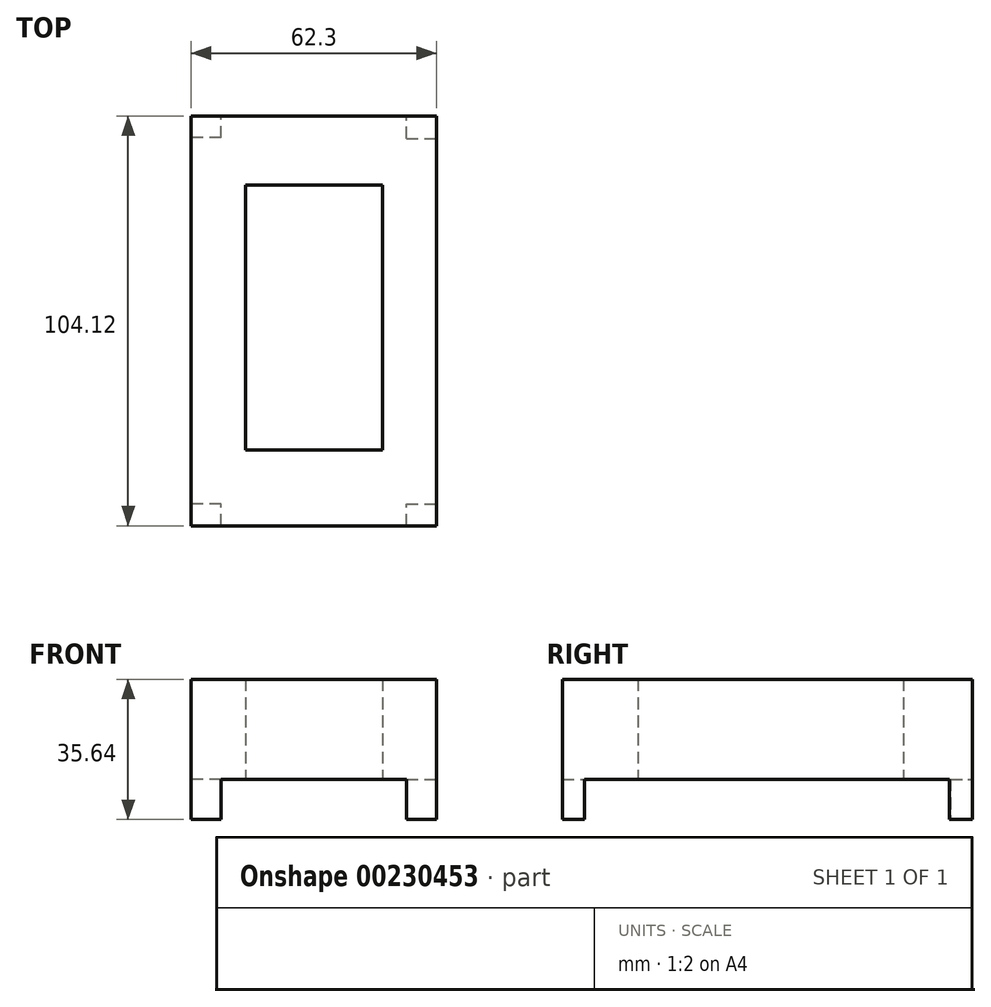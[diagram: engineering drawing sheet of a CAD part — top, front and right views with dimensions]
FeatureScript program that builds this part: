
annotation { "Feature Type Name" : "Feature", "Feature Type Description" : "" }
export const myFeature = defineFeature(function(context is Context, id is Id, definition is map)
    precondition{}
    {
        {
            var Q0;
            Q0=qCreatedBy(makeId("Top.planeOp"),FACE);
            var sketch = newSketch(context, id + "F0", { "sketchPlane" : qUnion([Q0])});
            skLineSegment(sketch, "E0.bottom", {"start": v(-17.28, 34.56) * mm, "end": v(17.5, 34.56) * mm});
            skLineSegment(sketch, "E0.top", {"start": v(-17.28, -32.86) * mm, "end": v(17.5, -32.86) * mm});
            skLineSegment(sketch, "E0.left", {"start": v(-17.28, 34.56) * mm, "end": v(-17.28, -32.86) * mm});
            skLineSegment(sketch, "E0.right", {"start": v(17.5, 34.56) * mm, "end": v(17.5, -32.86) * mm});
            skSolve(sketch);
        }
        {
            var Q0;
            Q0=qCreatedBy(makeId("Top.planeOp"),FACE);
            var sketch = newSketch(context, id + "F1", { "sketchPlane" : qUnion([Q0])});
            skLineSegment(sketch, "E1.bottom", {"start": v(31.15, -52.06) * mm, "end": v(-31.15, -52.06) * mm});
            skLineSegment(sketch, "E1.top", {"start": v(31.15, 52.06) * mm, "end": v(-31.15, 52.06) * mm});
            skLineSegment(sketch, "E1.left", {"start": v(31.15, -52.06) * mm, "end": v(31.15, 52.06) * mm});
            skLineSegment(sketch, "E1.right", {"start": v(-31.15, -52.06) * mm, "end": v(-31.15, 52.06) * mm});
            skPoint(sketch, "E1.middle", {"position": v(0, 0) * mm});
            skSolve(sketch);
        }
        {
            var Q0;
            Q0=makeQuery(id+"F1.imprint","IMPRINT",FACE,{"disambiguationData":[TD([[makeQuery(id+"F1.imprint","IMPRINT",EDGE,{"derivedFrom":sQuery(id+"F1.wireOp",EDGE,"E1.bottom")}),-1.0]])]});
            var sketch = newSketch(context, id + "F2", { "sketchPlane" : qUnion([Q0])});
            skSolve(sketch);
        }
        {
            var Q0;
            Q0=makeQuery(id+"F2.imprint","IMPRINT",FACE,{"disambiguationData":[TD([[makeQuery(id+"F2.imprint","IMPRINT",EDGE,{"derivedFrom":makeQuery(id+"F1.imprint","IMPRINT",EDGE,{"derivedFrom":sQuery(id+"F1.wireOp",EDGE,"E1.bottom")})}),-1.0]])]});
            var Q1;
            Q1=makeQuery(id+"F0.imprint","IMPRINT",FACE,{"disambiguationData":[TD([[makeQuery(id+"F0.imprint","IMPRINT",EDGE,{"derivedFrom":sQuery(id+"F0.wireOp",EDGE,"E0.bottom")}),-1.0]])]});
            extrude(context, id + "F3", {"entities" : qUnion([Q0, Q1]), "depth" : 25.4 * mm});
        }
        {
            var Q0;
            Q0=makeQuery(id+"F3.opExtrude","SWEPT_FACE",FACE,{"disambiguationData":[OSD([sQuery(id+"F1.wireOp",EDGE,"E1.left")])]});
            var sketch = newSketch(context, id + "F4", { "sketchPlane" : qUnion([Q0])});
            skLineSegment(sketch, "E2.bottom", {"start": v(-52.06, 0) * mm, "end": v(-46.51, 0) * mm});
            skLineSegment(sketch, "E2.top", {"start": v(-52.06, -10.24) * mm, "end": v(-46.51, -10.24) * mm});
            skLineSegment(sketch, "E2.left", {"start": v(-52.06, 0) * mm, "end": v(-52.06, -10.24) * mm});
            skLineSegment(sketch, "E2.right", {"start": v(-46.51, 0) * mm, "end": v(-46.51, -10.24) * mm});
            skLineSegment(sketch, "E3.bottom", {"start": v(52.06, 0) * mm, "end": v(46.3, 0) * mm});
            skLineSegment(sketch, "E3.top", {"start": v(52.06, -10.24) * mm, "end": v(46.3, -10.24) * mm});
            skLineSegment(sketch, "E3.left", {"start": v(52.06, 0) * mm, "end": v(52.06, -10.24) * mm});
            skLineSegment(sketch, "E3.right", {"start": v(46.3, 0) * mm, "end": v(46.3, -10.24) * mm});
            skSolve(sketch);
        }
        {
            var Q0;
            Q0 = qSketchRegion(id + "F4", true);
            extrude(context, id + "F5", {"entities" : qUnion([Q0]), "operationType" : NewBodyOperationType.ADD, "oppositeDirection" : true, "depth" : 7.62 * mm});
        }
        {
            var Q0;
            Q0=makeQuery(id+"F3.opExtrude","SWEPT_FACE",FACE,{"disambiguationData":[OSD([sQuery(id+"F1.wireOp",EDGE,"E1.right")])]});
            var sketch = newSketch(context, id + "F6", { "sketchPlane" : qUnion([Q0])});
            skLineSegment(sketch, "E4.bottom", {"start": v(-52.06, 0) * mm, "end": v(-46.51, 0) * mm});
            skLineSegment(sketch, "E4.top", {"start": v(-52.06, -10.24) * mm, "end": v(-46.51, -10.24) * mm});
            skLineSegment(sketch, "E4.left", {"start": v(-52.06, 0) * mm, "end": v(-52.06, -10.24) * mm});
            skLineSegment(sketch, "E4.right", {"start": v(-46.51, 0) * mm, "end": v(-46.51, -10.24) * mm});
            skLineSegment(sketch, "E5.bottom", {"start": v(52.06, 0) * mm, "end": v(46.51, 0) * mm});
            skLineSegment(sketch, "E5.top", {"start": v(52.06, -10.24) * mm, "end": v(46.51, -10.24) * mm});
            skLineSegment(sketch, "E5.left", {"start": v(52.06, 0) * mm, "end": v(52.06, -10.24) * mm});
            skLineSegment(sketch, "E5.right", {"start": v(46.51, 0) * mm, "end": v(46.51, -10.24) * mm});
            skSolve(sketch);
        }
        {
            var Q0;
            Q0 = qSketchRegion(id + "F6", true);
            extrude(context, id + "F7", {"entities" : qUnion([Q0]), "operationType" : NewBodyOperationType.ADD, "oppositeDirection" : true, "depth" : 7.62 * mm});
        }
    });
